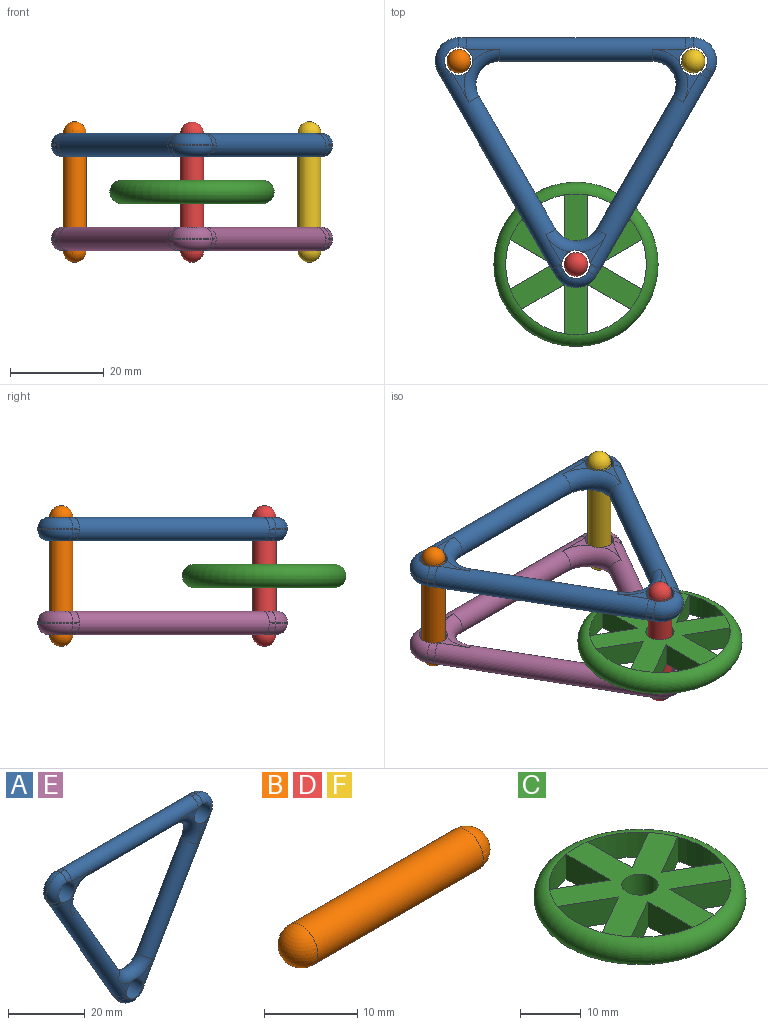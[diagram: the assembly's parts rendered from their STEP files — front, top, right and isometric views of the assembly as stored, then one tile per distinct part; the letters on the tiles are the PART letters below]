
ASSEMBLY  parts=6 mates=5
PART A: 48 faces, bbox 60.8x5.3x54.1 mm
  f0: plane 7x2.58mm, normal (0,-1,0), area 5.5mm2, adj f20,f38,f41
  f1: plane 6.19x3.5mm, normal (0,-1,0), area 5.5mm2, adj f20,f24,f38
  f2: plane 6.19x3.5mm, normal (0,-1,0), area 5.5mm2, adj f19,f32,f37
  f3: plane 7x2.58mm, normal (0,-1,0), area 5.5mm2, adj f19,f32,f41
  f4: plane 6.06x5.07mm, normal (0,-1,0), area 5.5mm2, adj f18,f24,f29
  f5: plane 1.44x0.83mm, normal (-0.87,0,-0.5), area 0.1mm2, adj f14,f34,f43
  f6: plane 1.44x0.83mm, normal (0.87,0,-0.5), area 0.1mm2, adj f16,f26,f30
  f7: plane 1.66x0.1mm, normal (0,0,1), area 0.1mm2, adj f21,f42,f46
  f8: plane 6.19x3.5mm, normal (0,1,0), area 5.5mm2, adj f20,f24,f38
  f9: plane 7x2.58mm, normal (0,1,0), area 5.5mm2, adj f20,f38,f41
  f10: plane 7x2.58mm, normal (0,1,0), area 5.5mm2, adj f19,f32,f41
  f11: plane 6.19x3.5mm, normal (0,1,0), area 5.5mm2, adj f19,f32,f37
  f12: plane 6.06x5.07mm, normal (0,1,0), area 5.5mm2, adj f18,f29,f37
  f13: plane 1.44x0.83mm, normal (-0.87,0,-0.5), area 0.1mm2, adj f21,f36,f45
  f14: cylinder r=5mm len=8.66mm, axis (0,1,0), area 1.1mm2, adj f5,f15,f27,f35
  f15: plane 1.44x0.83mm, normal (0.87,0,-0.5), area 0.1mm2, adj f14,f25,f28
  f16: cylinder r=5mm len=7.5mm, axis (0,1,0), area 1.1mm2, adj f6,f17,f31,f39
  f17: plane 1.66x0.1mm, normal (0,0,1), area 0.1mm2, adj f16,f40,f44
  f18: cylinder r=3mm len=6mm, axis (0,1,0), area 94.2mm2, adj f4,f12,f22,f23,f25,f27,f28,f29
  f19: cylinder r=3mm len=6mm, axis (0,1,0), area 94.2mm2, adj f2,f3,f10,f11,f32,f33,f36,f42
  f20: cylinder r=3mm len=6mm, axis (0,1,0), area 94.2mm2, adj f0,f1,f8,f9,f26,f30,f31,f38
  f21: cylinder r=5mm len=7.5mm, axis (0,1,0), area 1.1mm2, adj f7,f13,f33,f47
  f22: plane 6.06x5.07mm, normal (0,-1,0), area 5.5mm2, adj f18,f29,f37
  f23: plane 6.06x5.07mm, normal (0,1,0), area 5.5mm2, adj f18,f24,f29
  f24: cylinder r=2.5mm len=42.93mm, axis (-0.5,0,-0.87), area 623.3mm2, adj f1,f4,f8,f23,f25,f26,f28,f29
  f25: bspline ~3.2x2.89mm, area 5.9mm2, adj f15,f18,f24,f27
  f26: bspline ~3.46x3.16mm, area 5.9mm2, adj f6,f20,f24,f31
  f27: torus R=2.5mm, axis (0,-1,0), area 30.8mm2, adj f14,f18,f25,f34
  f28: bspline ~3.2x2.89mm, area 5.9mm2, adj f15,f18,f24,f35
  f29: torus R=7.5mm, axis (0,-1,0), area 95.3mm2, adj f4,f12,f18,f22,f23,f24,f37
  f30: bspline ~3.46x3.16mm, area 5.9mm2, adj f6,f20,f24,f39
  f31: torus R=2.5mm, axis (0,-1,0), area 30.8mm2, adj f16,f20,f26,f40
  f32: torus R=7.5mm, axis (0,-1,0), area 96.2mm2, adj f2,f3,f10,f11,f19,f37,f41
  f33: torus R=2.5mm, axis (0,-1,0), area 30.8mm2, adj f19,f21,f36,f42
  f34: bspline ~3.2x2.89mm, area 5.9mm2, adj f5,f18,f27,f37
  f35: torus R=2.5mm, axis (0,1,0), area 30.8mm2, adj f14,f18,f28,f43
  f36: bspline ~3.46x3.16mm, area 5.9mm2, adj f13,f19,f33,f37
  f37: cylinder r=2.5mm len=42.93mm, axis (0.5,0,-0.87), area 623.3mm2, adj f2,f11,f12,f22,f29,f32,f34,f36
  f38: torus R=7.5mm, axis (0,-1,0), area 96.2mm2, adj f0,f1,f8,f9,f20,f24,f41
  f39: torus R=2.5mm, axis (0,1,0), area 30.8mm2, adj f16,f20,f30,f44
  f40: bspline ~2.68x2.66mm, area 5.9mm2, adj f17,f20,f31,f41
  f41: cylinder r=2.5mm len=46.68mm, axis (-1,0,0), area 623.3mm2, adj f0,f3,f9,f10,f32,f38,f40,f42
  f42: bspline ~2.68x2.66mm, area 5.9mm2, adj f7,f19,f33,f41
  f43: bspline ~3.2x2.89mm, area 5.9mm2, adj f5,f18,f35,f37
  f44: bspline ~2.68x2.66mm, area 5.9mm2, adj f17,f20,f39,f41
  f45: bspline ~3.46x3.16mm, area 5.9mm2, adj f13,f19,f37,f47
  f46: bspline ~2.68x2.66mm, area 5.9mm2, adj f7,f19,f41,f47
  f47: torus R=2.5mm, axis (0,1,0), area 30.8mm2, adj f19,f21,f45,f46
PART B: 3 faces, bbox 30x5x5 mm
  f0: sphere r=2.5mm, area 39.3mm2, adj f1
  f1: cylinder r=2.5mm len=25mm, axis (1,0,0), area 392.7mm2, adj f0,f2
  f2: sphere r=2.5mm, area 39.3mm2, adj f1
PART C: 22 faces, bbox 37.9x37.9x5 mm
  f0: cylinder r=15mm len=10.46mm, axis (0,0,-1), area 53.4mm2, adj f1,f12,f21
  f1: plane 9.06x5.23mm, normal (0.5,0.87,0), area 52.3mm2, adj f0,f12,f19,f20
  f2: cylinder r=15mm len=9.06mm, axis (0,0,-1), area 53.4mm2, adj f3,f13,f21
  f3: plane 10.46x5mm, normal (1,0,0), area 52.3mm2, adj f2,f13,f19,f20
  f4: cylinder r=15mm len=9.06mm, axis (0,0,-1), area 53.4mm2, adj f5,f14,f21
  f5: plane 9.06x5.23mm, normal (0.5,-0.87,0), area 52.3mm2, adj f4,f14,f19,f20
  f6: cylinder r=15mm len=10.46mm, axis (0,0,-1), area 53.4mm2, adj f7,f15,f21
  f7: plane 9.06x5.23mm, normal (-0.5,-0.87,0), area 52.3mm2, adj f6,f15,f19,f20
  f8: cylinder r=15mm len=9.06mm, axis (0,0,-1), area 53.4mm2, adj f9,f16,f21
  f9: plane 9.06x5.23mm, normal (-0.5,0.87,0), area 52.3mm2, adj f8,f16,f19,f20
  f10: plane 10.46x5mm, normal (-1,0,0), area 52.3mm2, adj f11,f17,f19,f20
  f11: plane 9.06x5.23mm, normal (0.5,0.87,0), area 52.3mm2, adj f10,f17,f19,f20
  f12: plane 9.06x5.23mm, normal (0.5,-0.87,0), area 52.3mm2, adj f0,f1,f19,f20
  f13: plane 9.06x5.23mm, normal (-0.5,-0.87,0), area 52.3mm2, adj f2,f3,f19,f20
  f14: plane 10.46x5mm, normal (-1,0,0), area 52.3mm2, adj f4,f5,f19,f20
  f15: plane 9.06x5.23mm, normal (-0.5,0.87,0), area 52.3mm2, adj f6,f7,f19,f20
  f16: plane 10.46x5mm, normal (1,0,0), area 52.3mm2, adj f8,f9,f19,f20
  f17: cylinder r=15mm len=9.06mm, axis (0,0,-1), area 53.4mm2, adj f10,f11,f21
  f18: cylinder r=3mm len=6mm, axis (0,0,-1), area 94.2mm2, adj f19,f20
  f19: plane 30x28.12mm, normal (0,0,1), area 354.7mm2, adj f1,f3,f5,f7,f9,f10,f11,f12
  f20: plane 30x28.12mm, normal (0,0,-1), area 354.7mm2, adj f1,f3,f5,f7,f9,f10,f11,f12
  f21: torus R=15mm, axis (0,0,1), area 818.8mm2, adj f0,f2,f4,f6,f8,f17,f19,f20
PART D: same geometry as B
PART E: same geometry as A
PART F: same geometry as B
PLACE A rot(axis=(-1,0,0),90deg) t=(-37.8,-2.2,21.43)mm
PLACE B rot(axis=(0,1,0),90deg) t=(-63.19,30.32,13.93)mm
PLACE C t=(-35.69,-12.98,11.43)mm
PLACE D rot(axis=(0,1,0),90deg) t=(-38.19,-12.98,13.93)mm
PLACE E rot(axis=(-1,0,0),90deg) t=(-37.8,-2.2,1.43)mm
PLACE F rot(axis=(0.71,0,0.71),180deg) t=(-13.19,30.32,13.93)mm
MATE fastened D.f1 <-> A.f14  axis (0,0,1) through (-35.69,-12.98,26.43)mm
MATE fastened D.f1 <-> E.f14  axis (0,0,-1) through (-35.69,-12.98,1.43)mm
MATE fastened B.f1 <-> A.f19  axis (0,0,1) through (-60.69,30.32,26.43)mm
MATE fastened C.f0 <-> D.f1  axis (0,0,-1) through (-35.69,-12.98,13.93)mm
MATE fastened F.f1 <-> A.f16  axis (0,0,1) through (-10.69,30.32,26.43)mm
